# Revit family: Building-IEC309Connections-GEWISS-IEC309BTS-10°_SURF-MOUNT_SOCKET_20-25V_IP44
name_source: partatom
category: Apparecchi elettrici
units: mm (PartAtom-declared; Revit-internal decimal feet)

## family parameters
Condiviso = Sì
Host = Superficie
Mantenere orientamento annotazione = Sì
Punto di calcolo locali = Sì
Quota connettore circolare = Usa diametro
Taglio con vuoti quando caricato = No
Tipo di parte = Normale

## types (18) — shared parameters
BLOCCO = B=C
Catalogue = BUILDING
Corpo centrale = Default(2)
Electrocod = 2210
FORMULA = 1000 mm  [stored 3.28084 ft]
Glow wire test: = 850 °C (active parts) - 650 °C (passive parts)
IDF = e79ba3c3-8da5-485c-af05-0b86c567b159
IDT = 985099ec4f384df9a4f1881abc1748ff
IP degree = IP44
Immagine tipo = <Nessuno>
Insulation resistance = - 10 M?
L = 155 mm
Operating temperature: = -25 +40 °C
Piastra = Default(2)
Produttore = GEWISS S.p.A.
Prospetto di default = 500 mm
SEO = Socket outlet
SPinotto = Default(2)
Shock resistance = IK08
Sportello_visibile = Sì
Spostamento_S = 955 mm
Technical sheet = https://www.gewiss.com
Thermo-pressure with ball = 125 °C (active parts) - 80 °C (passive parts)
Type of wiring = With screw
Typology = 10° angled surface-mounting socket-outlet
URL = https://www.gewiss.com
Version file RFA = 21.11
W = 115 mm

## per-type parameters (varying)
| type | Breaking capacity at 1.1 Un | Colour: | Descrizione | Frequency | Modello | No. of poles | Permissible overload | Rated current (A) | Rated voltage: | Reference h: | Terminal tightening capacity | Total number of operations |
| GW62457 - IP44 10°W.RECEPTACLE 3P 16A 24V N.R. | 20A | Violet | IP44 10°W.RECEPTACLE 3P 16A 24V N.R. | 50 - 60 Hz | GW62457 | 3P | 22A | 16 | 20-25 V | - | 1-2.5mm² flexible cables - 1.5-4mm² rigid cables | -5000 |
| GW62468 - IP44 10°W.RECEPTACLE 3P 32A 42V 12H | 40A | White | IP44 10°W.RECEPTACLE 3P 32A 42V 12H | 50 - 60 Hz | GW62468 | 3P | 42A | 32 | 40-50 V | 12 | 2.5-6mm² flexible cables - 2.5-10mm² rigid cables | -2000 |
| GW62456 - IP44 10°W.RECEPTACLE 2P 16A 24V N.R. | 20A | Violet | IP44 10°W.RECEPTACLE 2P 16A 24V N.R. | 50 - 60 Hz | GW62456 | 2P | 22A | 16 | 20-25 V | - | 1-2.5mm² flexible cables - 1.5-4mm² rigid cables | -5000 |
| GW62470 - IP44 10°W.RECEPTACLE 3P 32A 24/42V4H | 40A | Green | IP44 10°W.RECEPTACLE 3P 32A 24/42V4H | 100 - 200 Hz | GW62470 | 3P | 42A | 32 | 20-25V and 40-50 V | 4 | 2.5-6mm² flexible cables - 2.5-10mm² rigid cables | -2000 |
| GW62466 - IP44 10°W.RECEPTACLE 3P 32A 24V N.R. | 40A | Violet | IP44 10°W.RECEPTACLE 3P 32A 24V N.R. | 50 - 60 Hz | GW62466 | 3P | 42A | 32 | 20-25 V | - | 2.5-6mm² flexible cables - 2.5-10mm² rigid cables | -2000 |
| GW62464 - IP44 10°W.RECEPTACLE 2P 16A CC 10H | 20A | White | IP44 10°W.RECEPTACLE 2P 16A CC 10H | d.c. | GW62464 | 2P | 22A | 16 | 20-25V and 40-50 V | 10 | 1-2.5mm² flexible cables - 1.5-4mm² rigid cables | -5000 |
| GW62472 - IP44 10°W.RECEPTACLE 3P 32A 24/42V 11H | 40A | Green | IP44 10°W.RECEPTACLE 3P 32A 24/42V 11H | 401 - 500 Hz | GW62472 | 3P | 42A | 32 | 20-25V and 40-50 V | 11 | 2.5-6mm² flexible cables - 2.5-10mm² rigid cables | -2000 |
| GW62459 - IP44 10°W.RECEPTACLE 3P 16A 42V 12H | 20A | White | IP44 10°W.RECEPTACLE 3P 16A 42V 12H | 50 - 60 Hz | GW62459 | 3P | 22A | 16 | 40-50 V | 12 | 1-2.5mm² flexible cables - 1.5-4mm² rigid cables | -5000 |
| GW62469 - IP44 10°W.RECEPTACLE 2P 32A 24/42V4H | 40A | Green | IP44 10°W.RECEPTACLE 2P 32A 24/42V4H | 100 - 200 Hz | GW62469 | 2P | 42A | 32 | 20-25V and 40-50 V | 4 | 2.5-6mm² flexible cables - 2.5-10mm² rigid cables | -2000 |
| GW62465 - IP44 10°W.RECEPTACLE 2P 32A 24V N.R. | 40A | Violet | IP44 10°W.RECEPTACLE 2P 32A 24V N.R. | 50 - 60 Hz | GW62465 | 2P | 42A | 32 | 20-25 V | - | 2.5-6mm² flexible cables - 2.5-10mm² rigid cables | -2000 |
| GW62458 - IP44 10°W.RECEPTACLE 2P 16A 42V 12H | 20A | White | IP44 10°W.RECEPTACLE 2P 16A 42V 12H | 50 - 60 Hz | GW62458 | 2P | 22A | 16 | 40-50 V | 12 | 1-2.5mm² flexible cables - 1.5-4mm² rigid cables | -5000 |
| GW62462 - IP44 10°W.RECEPTACLE 2P 16A 24/42V 11H | 20A | Green | IP44 10°W.RECEPTACLE 2P 16A 24/42V 11H | 401 - 500 Hz | GW62462 | 2P | 22A | 16 | 20-25V and 40-50 V | 11 | 1-2.5mm² flexible cables - 1.5-4mm² rigid cables | -5000 |
| GW62471 - IP44 10°W.RECEPTACLE 2P 32A 24/42V 11H | 40A | Green | IP44 10°W.RECEPTACLE 2P 32A 24/42V 11H | 401 - 500 Hz | GW62471 | 2P | 42A | 32 | 20-25V and 40-50 V | 11 | 2.5-6mm² flexible cables - 2.5-10mm² rigid cables | -2000 |
| GW62467 - IP44 10°W.RECEPTACLE 2P 32A 42V 12H | 40A | White | IP44 10°W.RECEPTACLE 2P 32A 42V 12H | 50 - 60 Hz | GW62467 | 2P | 42A | 32 | 40-50 V | 12 | 2.5-6mm² flexible cables - 2.5-10mm² rigid cables | -2000 |
| GW62463 - IP44 10°W.RECEPTACLE 3P 16A 24/42V 11H | 20A | Green | IP44 10°W.RECEPTACLE 3P 16A 24/42V 11H | 401 - 500 Hz | GW62463 | 3P | 22A | 16 | 20-25V and 40-50 V | 11 | 1-2.5mm² flexible cables - 1.5-4mm² rigid cables | -5000 |
| GW62473 - IP44 10°W.RECEPTACLE 2P 32A CC 10H | 40A | White | IP44 10°W.RECEPTACLE 2P 32A CC 10H | d.c. | GW62473 | 2P | 42A | 32 | 20-25V and 40-50 V | 10 | 2.5-6mm² flexible cables - 2.5-10mm² rigid cables | -2000 |
| GW62461 - IP44 10°W.RECEPTACLE 3P 16A 24/42V 4H | 20A | Green | IP44 10°W.RECEPTACLE 3P 16A 24/42V 4H | 100 - 200 Hz | GW62461 | 3P | 22A | 16 | 20-25V and 40-50 V | 4 | 1-2.5mm² flexible cables - 1.5-4mm² rigid cables | -5000 |
| GW62460 - IP44 10°W.RECEPTACLE 2P 16A 24/42V 4H | 20A | Green | IP44 10°W.RECEPTACLE 2P 16A 24/42V 4H | 100 - 200 Hz | GW62460 | 2P | 22A | 16 | 20-25V and 40-50 V | 4 | 1-2.5mm² flexible cables - 1.5-4mm² rigid cables | -5000 |

note: [stored X ft] marks values corroborated as IEEE doubles in the binary element streams (Revit-internal decimal feet)

## geometry (parser evidence)
native form markers: Sweep x1
no freeform markers — native parametric forms only
